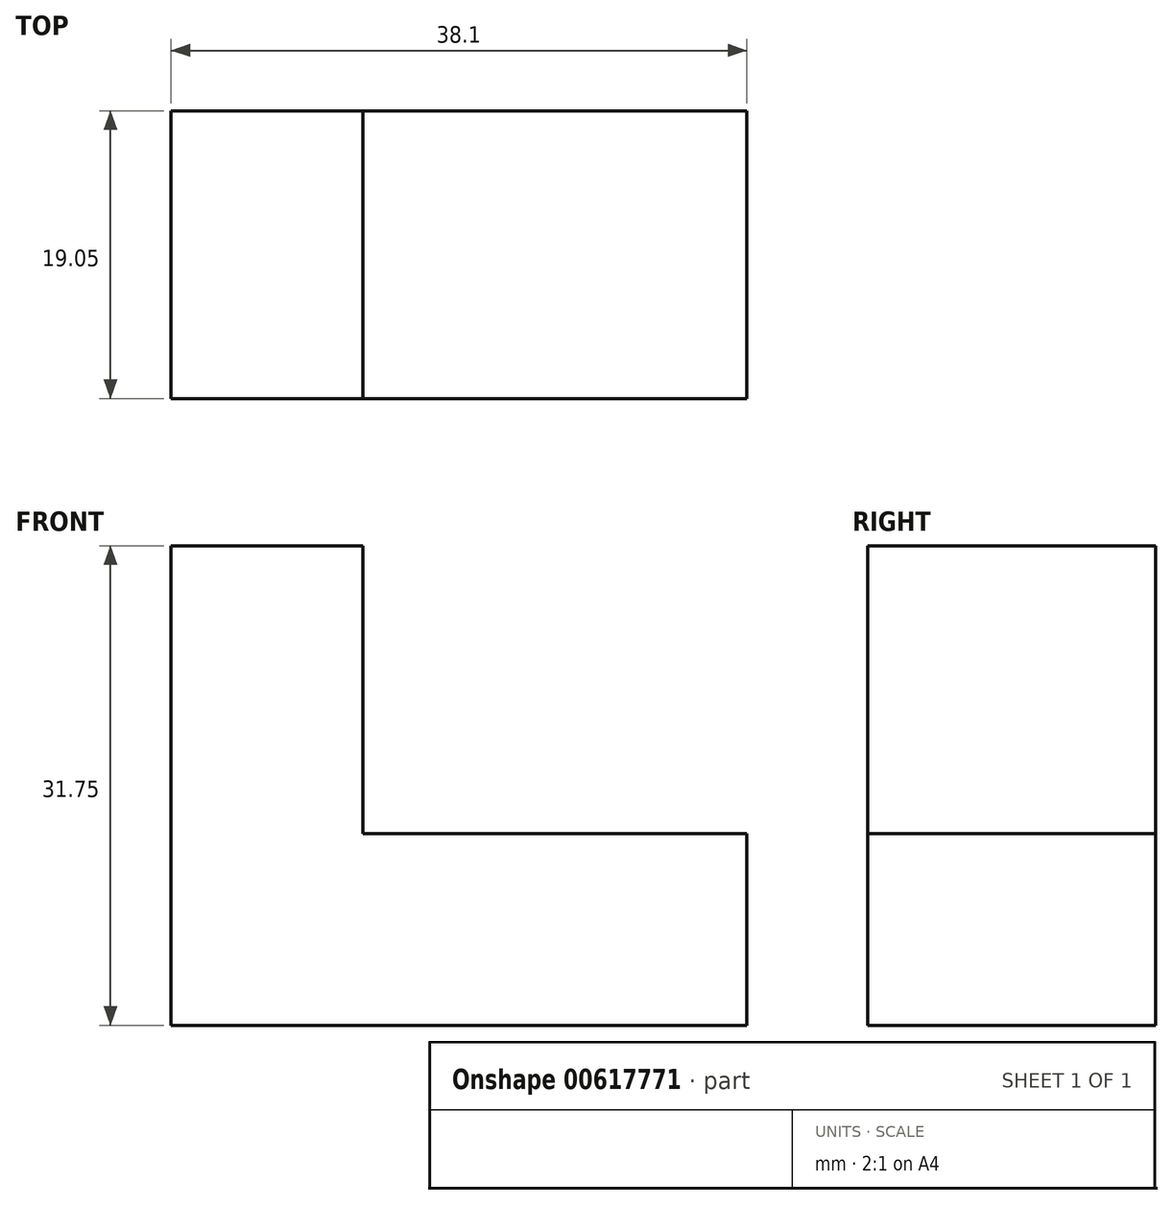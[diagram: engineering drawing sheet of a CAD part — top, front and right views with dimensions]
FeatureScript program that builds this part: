
annotation { "Feature Type Name" : "Feature", "Feature Type Description" : "" }
export const myFeature = defineFeature(function(context is Context, id is Id, definition is map)
    precondition{}
    {
        {
            var Q0;
            Q0=qCreatedBy(makeId("Front.planeOp"),FACE);
            var sketch = newSketch(context, id + "F0", { "sketchPlane" : qUnion([Q0])});
            skLineSegment(sketch, "E0", {"start": v(0, 31.75) * mm, "end": v(0, 0) * mm});
            skLineSegment(sketch, "E1", {"start": v(0, 0) * mm, "end": v(38.1, 0) * mm});
            skLineSegment(sketch, "E2", {"start": v(38.1, 0) * mm, "end": v(38.1, 12.7) * mm});
            skLineSegment(sketch, "E3", {"start": v(38.1, 12.7) * mm, "end": v(12.7, 12.7) * mm});
            skLineSegment(sketch, "E4", {"start": v(12.7, 12.7) * mm, "end": v(12.7, 31.75) * mm});
            skLineSegment(sketch, "E5", {"start": v(12.7, 31.75) * mm, "end": v(0, 31.75) * mm});
            skSolve(sketch);
        }
        {
            var Q0;
            Q0 = qSketchRegion(id + "F0", true);
            extrude(context, id + "F1", {"entities" : qUnion([Q0]), "depth" : 19.05 * mm, "offsetDistance" : 25.4 * mm});
        }
    });
